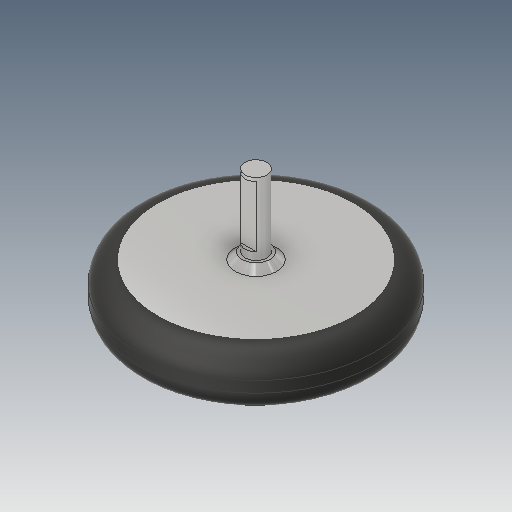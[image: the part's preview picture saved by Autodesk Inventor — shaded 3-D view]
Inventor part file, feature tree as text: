
AUTODESK INVENTOR PART (.ipt)
format: ipt  version: 2018 (Build 220112000, 112)  size: 165,376 bytes
history: native  units: in
note: dims shown in document units (in); Inventor stores cm internally (conversion verified against a paired STEP export)
features: other x3, sketch x3
ambient origin geometry x8: Origin, YZ Plane, XZ Plane, XY Plane, X Axis, Y Axis, Z Axis, Center Point
bodies: Solid1 (feature_tree)
feature tree (6):
  other  "10-001-ACTR_MIR.ipt"
  other  "Solid1::10-001-ACTR_MIR.ipt"
  other  "TaggingFeature1"
  sketch  "Sketch1"  dims[d0=0.3937in]
  sketch  "Sketch2"
  sketch  "Sketch3"
